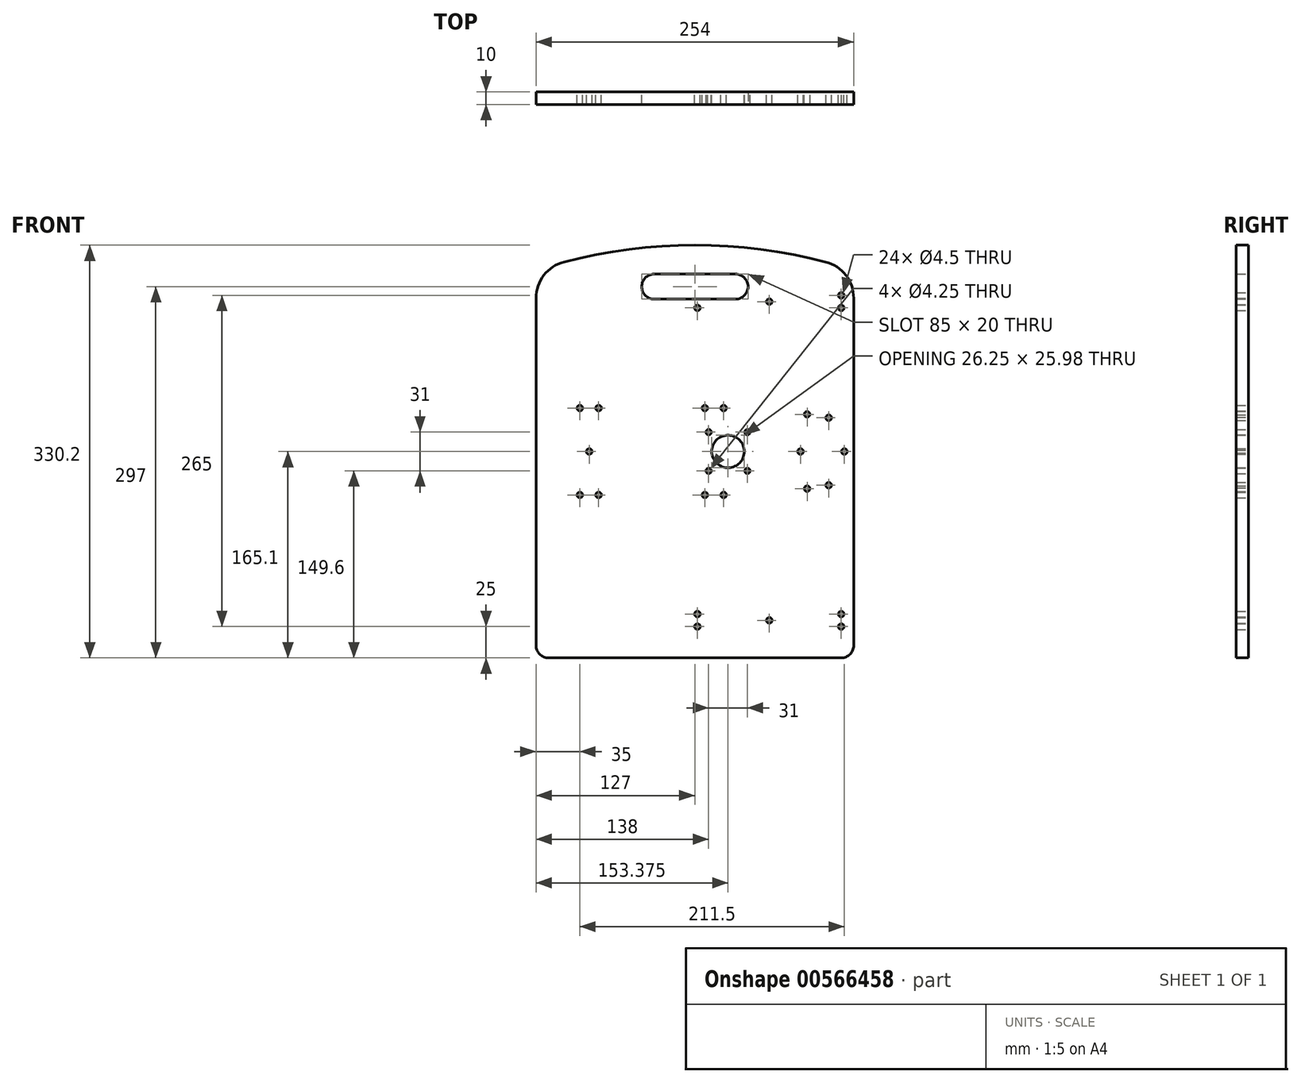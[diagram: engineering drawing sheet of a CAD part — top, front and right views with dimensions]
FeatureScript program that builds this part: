
annotation { "Feature Type Name" : "Feature", "Feature Type Description" : "" }
export const myFeature = defineFeature(function(context is Context, id is Id, definition is map)
    precondition{}
    {
        {
            var Q0;
            Q0=qCreatedBy(makeId("Front.planeOp"),FACE);
            var sketch = newSketch(context, id + "F0", { "sketchPlane" : qUnion([Q0])});
            skLineSegment(sketch, "E0.bottom", {"start": v(127, -165.1) * mm, "end": v(-127, -165.1) * mm});
            skLineSegment(sketch, "E0.top", {"start": v(127, 165.1) * mm, "end": v(-127, 165.1) * mm, "construction": true});
            skLineSegment(sketch, "E0.left", {"start": v(127, -165.1) * mm, "end": v(127, 145.1) * mm});
            skLineSegment(sketch, "E0.right", {"start": v(-127, -165.1) * mm, "end": v(-127, 145.1) * mm});
            skPoint(sketch, "E0.middle", {"position": v(0, 0) * mm});
            skLineSegment(sketch, "E1.bottom", {"start": v(42.5, 121.9) * mm, "end": v(-42.5, 121.9) * mm});
            skLineSegment(sketch, "E1.top", {"start": v(42.5, 141.9) * mm, "end": v(-42.5, 141.9) * mm});
            skLineSegment(sketch, "E1.left", {"start": v(42.5, 121.9) * mm, "end": v(42.5, 141.9) * mm});
            skLineSegment(sketch, "E1.right", {"start": v(-42.5, 121.9) * mm, "end": v(-42.5, 141.9) * mm});
            skPoint(sketch, "E1.middle", {"position": v(0, 131.9) * mm});
            skArc(sketch, "E2", {"start": v(127, 145.1) * mm, "mid": v(0, 165.1) * mm, "end": v(-127, 145.1) * mm});
            skLineSegment(sketch, "E3.bottom", {"start": v(-77, -34.75) * mm, "end": v(-92, -34.75) * mm, "construction": true});
            skLineSegment(sketch, "E3.top", {"start": v(-77, 34.75) * mm, "end": v(-92, 34.75) * mm, "construction": true});
            skLineSegment(sketch, "E3.left", {"start": v(-77, -34.75) * mm, "end": v(-77, 34.75) * mm, "construction": true});
            skLineSegment(sketch, "E3.right", {"start": v(-92, -34.75) * mm, "end": v(-92, 34.75) * mm, "construction": true});
            skPoint(sketch, "E3.middle", {"position": v(-84.5, 0) * mm});
            skCircle(sketch, "E4", {"center": v(-92, 34.75) * mm, "radius": 2.25 * mm});
            skCircle(sketch, "E5", {"center": v(-77, 34.75) * mm, "radius": 2.25 * mm});
            skCircle(sketch, "E6", {"center": v(-77, -34.75) * mm, "radius": 2.25 * mm});
            skCircle(sketch, "E7", {"center": v(-92, -34.75) * mm, "radius": 2.25 * mm});
            skCircle(sketch, "E8.MirrorC", {"center": v(77, 34.75) * mm, "radius": 2.25 * mm, "construction": true});
            skCircle(sketch, "E9.MirrorC", {"center": v(92, 34.75) * mm, "radius": 2.25 * mm, "construction": true});
            skCircle(sketch, "E10.MirrorC", {"center": v(77, -34.75) * mm, "radius": 2.25 * mm, "construction": true});
            skCircle(sketch, "E11.MirrorC", {"center": v(92, -34.75) * mm, "radius": 2.25 * mm, "construction": true});
            skPoint(sketch, "E12.MirrorP", {"position": v(84.5, 0) * mm});
            skLineSegment(sketch, "E13.MirrorCS", {"start": v(92, -34.75) * mm, "end": v(92, 34.75) * mm, "construction": true});
            skLineSegment(sketch, "E14.MirrorCS", {"start": v(77, -34.75) * mm, "end": v(77, 34.75) * mm, "construction": true});
            skLineSegment(sketch, "E15.MirrorCS", {"start": v(77, 34.75) * mm, "end": v(92, 34.75) * mm, "construction": true});
            skLineSegment(sketch, "E16.MirrorCS", {"start": v(77, -34.75) * mm, "end": v(92, -34.75) * mm, "construction": true});
            skLineSegment(sketch, "E17.bottom", {"start": v(117, -140.1) * mm, "end": v(2, -140.1) * mm, "construction": true});
            skLineSegment(sketch, "E17.top", {"start": v(117, -130.1) * mm, "end": v(2, -130.1) * mm, "construction": true});
            skLineSegment(sketch, "E17.left", {"start": v(117, -140.1) * mm, "end": v(117, -130.1) * mm, "construction": true});
            skLineSegment(sketch, "E17.right", {"start": v(2, -140.1) * mm, "end": v(2, -130.1) * mm, "construction": true});
            skPoint(sketch, "E17.middle", {"position": v(59.5, -135.1) * mm});
            skCircle(sketch, "E18", {"center": v(2, -130.1) * mm, "radius": 2.25 * mm});
            skCircle(sketch, "E19", {"center": v(117, -140.1) * mm, "radius": 2.25 * mm});
            skCircle(sketch, "E20", {"center": v(117, -130.1) * mm, "radius": 2.25 * mm});
            skCircle(sketch, "E21", {"center": v(2, -140.1) * mm, "radius": 2.25 * mm});
            skCircle(sketch, "E22.MirrorC", {"center": v(117, 140.1) * mm, "radius": 2.25 * mm, "construction": true});
            skCircle(sketch, "E23.MirrorC", {"center": v(117, 130.1) * mm, "radius": 2.25 * mm, "construction": true});
            skLineSegment(sketch, "E24.MirrorCS", {"start": v(117, 140.1) * mm, "end": v(117, 130.1) * mm, "construction": true});
            skCircle(sketch, "E25.MirrorC", {"center": v(2, 140.1) * mm, "radius": 2.25 * mm, "construction": true});
            skLineSegment(sketch, "E26.MirrorCS", {"start": v(2, 140.1) * mm, "end": v(2, 130.1) * mm, "construction": true});
            skCircle(sketch, "E27.MirrorC", {"center": v(2, 130.1) * mm, "radius": 2.25 * mm, "construction": true});
            skLineSegment(sketch, "E28.MirrorCS", {"start": v(117, 140.1) * mm, "end": v(2, 140.1) * mm, "construction": true});
            skLineSegment(sketch, "E29.MirrorCS", {"start": v(117, 130.1) * mm, "end": v(2, 130.1) * mm, "construction": true});
            skPoint(sketch, "E30.MirrorP", {"position": v(59.5, 135.1) * mm});
            skCircle(sketch, "E31", {"center": v(-84.5, 0) * mm, "radius": 2.25 * mm});
            skCircle(sketch, "E32.MirrorC", {"center": v(84.5, 0) * mm, "radius": 2.25 * mm});
            skCircle(sketch, "E33", {"center": v(-27, -145.1) * mm, "radius": 2.25 * mm, "construction": true});
            skCircle(sketch, "E34.MirrorC", {"center": v(27, -145.1) * mm, "radius": 2.25 * mm, "construction": true});
            skLineSegment(sketch, "E35", {"start": v(50, 0) * mm, "end": v(50, -46.74) * mm, "construction": true});
            skCircle(sketch, "E36.MirrorC", {"center": v(8, 34.75) * mm, "radius": 2.25 * mm});
            skCircle(sketch, "E37.MirrorC", {"center": v(23, 34.75) * mm, "radius": 2.25 * mm});
            skCircle(sketch, "E38.MirrorC", {"center": v(8, -34.75) * mm, "radius": 2.25 * mm});
            skCircle(sketch, "E39.MirrorC", {"center": v(23, -34.75) * mm, "radius": 2.25 * mm});
            skCircle(sketch, "E40.MirrorC", {"center": v(15.5, 0) * mm, "radius": 2.25 * mm});
            skLineSegment(sketch, "E41.MirrorCS", {"start": v(23, -34.75) * mm, "end": v(23, 34.75) * mm, "construction": true});
            skLineSegment(sketch, "E42.MirrorCS", {"start": v(8, -34.75) * mm, "end": v(8, 34.75) * mm, "construction": true});
            skLineSegment(sketch, "E43.MirrorCS", {"start": v(23, -34.75) * mm, "end": v(8, -34.75) * mm, "construction": true});
            skLineSegment(sketch, "E44.MirrorCS", {"start": v(23, 34.75) * mm, "end": v(8, 34.75) * mm, "construction": true});
            skCircle(sketch, "E45", {"center": v(107, 27) * mm, "radius": 2.25 * mm});
            skCircle(sketch, "E46.MirrorC", {"center": v(107, -27) * mm, "radius": 2.25 * mm});
            skCircle(sketch, "E47", {"center": v(59.5, -135.1) * mm, "radius": 2.25 * mm});
            skCircle(sketch, "E48.MirrorC", {"center": v(59.5, 135.1) * mm, "radius": 2.25 * mm, "construction": true});
            skLineSegment(sketch, "E49.bottom", {"start": v(42, -15.5) * mm, "end": v(11, -15.5) * mm, "construction": true});
            skLineSegment(sketch, "E49.top", {"start": v(42, 15.5) * mm, "end": v(11, 15.5) * mm, "construction": true});
            skLineSegment(sketch, "E49.left", {"start": v(42, -15.5) * mm, "end": v(42, 15.5) * mm, "construction": true});
            skLineSegment(sketch, "E49.right", {"start": v(11, -15.5) * mm, "end": v(11, 15.5) * mm, "construction": true});
            skPoint(sketch, "E49.middle", {"position": v(26.5, 0) * mm});
            skCircle(sketch, "E50", {"center": v(11, 15.5) * mm, "radius": 2.12 * mm});
            skCircle(sketch, "E51", {"center": v(42, 15.5) * mm, "radius": 2.12 * mm});
            skCircle(sketch, "E52", {"center": v(42, -15.5) * mm, "radius": 2.12 * mm});
            skCircle(sketch, "E53", {"center": v(11, -15.5) * mm, "radius": 2.12 * mm});
            skCircle(sketch, "E54", {"center": v(26.5, 0) * mm, "radius": 13 * mm});
            skCircle(sketch, "E55", {"center": v(119.5, 0) * mm, "radius": 2.25 * mm});
            skCircle(sketch, "E56", {"center": v(89.75, -29.75) * mm, "radius": 2.25 * mm});
            skCircle(sketch, "E57.MirrorC", {"center": v(89.75, 29.75) * mm, "radius": 2.25 * mm});
            skLineSegment(sketch, "E58.bottom", {"start": v(117, 124.9) * mm, "end": v(2, 124.9) * mm, "construction": true});
            skLineSegment(sketch, "E58.top", {"start": v(117, 114.9) * mm, "end": v(2, 114.9) * mm, "construction": true});
            skLineSegment(sketch, "E58.left", {"start": v(117, 124.9) * mm, "end": v(117, 114.9) * mm, "construction": true});
            skLineSegment(sketch, "E58.right", {"start": v(2, 124.9) * mm, "end": v(2, 114.9) * mm, "construction": true});
            skPoint(sketch, "E58.middle", {"position": v(59.5, 119.9) * mm});
            skCircle(sketch, "E59", {"center": v(2, 124.9) * mm, "radius": 2.25 * mm});
            skCircle(sketch, "E60", {"center": v(2, 114.9) * mm, "radius": 2.25 * mm});
            skCircle(sketch, "E61", {"center": v(117, 124.9) * mm, "radius": 2.25 * mm});
            skCircle(sketch, "E62", {"center": v(117, 114.9) * mm, "radius": 2.25 * mm});
            skCircle(sketch, "E63", {"center": v(59.5, 119.9) * mm, "radius": 2.25 * mm});
            skSolve(sketch);
        }
        {
            var Q0;
            Q0=qSketchRegion(id+"F0",true);
            extrude(context, id + "F1", {"entities" : qUnion([Q0]), "endBound" : BoundingType.SYMMETRIC, "depth" : 10 * mm});
        }
        {
            var Q0;
            Q0=makeQuery(id+"F1.opExtrude","SWEPT_EDGE",EDGE,{"disambiguationData":[OSD([sQuery(id+"F0.wireOp",EDGE,"E0.bottom"),sQuery(id+"F0.wireOp",EDGE,"E0.right")])]});
            var Q1;
            Q1=makeQuery(id+"F1.opExtrude","SWEPT_EDGE",EDGE,{"disambiguationData":[OSD([sQuery(id+"F0.wireOp",EDGE,"E0.bottom"),sQuery(id+"F0.wireOp",EDGE,"E0.left")])]});
            var Q2;
            Q2=makeQuery(id+"F1.opExtrude","SWEPT_EDGE",EDGE,{"disambiguationData":[OSD([sQuery(id+"F0.wireOp",EDGE,"E1.top"),sQuery(id+"F0.wireOp",EDGE,"E1.right")])]});
            var Q3;
            Q3=makeQuery(id+"F1.opExtrude","SWEPT_EDGE",EDGE,{"disambiguationData":[OSD([sQuery(id+"F0.wireOp",EDGE,"E1.bottom"),sQuery(id+"F0.wireOp",EDGE,"E1.right")])]});
            var Q4;
            Q4=makeQuery(id+"F1.opExtrude","SWEPT_EDGE",EDGE,{"disambiguationData":[OSD([sQuery(id+"F0.wireOp",EDGE,"E1.top"),sQuery(id+"F0.wireOp",EDGE,"E1.left")])]});
            var Q5;
            Q5=makeQuery(id+"F1.opExtrude","SWEPT_EDGE",EDGE,{"disambiguationData":[OSD([sQuery(id+"F0.wireOp",EDGE,"E1.bottom"),sQuery(id+"F0.wireOp",EDGE,"E1.left")])]});
            fillet(context, id + "F2", {"entities" : qUnion([Q0, Q1, Q2, Q3, Q4, Q5]), "radius" : 10 * mm, "tangentPropagation" : true, "allowEdgeOverflow" : false});
        }
        {
            var Q0;
            Q0=makeQuery(id+"F1.opExtrude","SWEPT_EDGE",EDGE,{"disambiguationData":[OSD([sQuery(id+"F0.wireOp",EDGE,"E0.left"),sQuery(id+"F0.wireOp",EDGE,"E2")])]});
            var Q1;
            Q1=makeQuery(id+"F1.opExtrude","SWEPT_EDGE",EDGE,{"disambiguationData":[OSD([sQuery(id+"F0.wireOp",EDGE,"E0.right"),sQuery(id+"F0.wireOp",EDGE,"E2")])]});
            fillet(context, id + "F3", {"entities" : qUnion([Q0, Q1]), "radius" : 30 * mm, "tangentPropagation" : true, "allowEdgeOverflow" : false});
        }
    });
